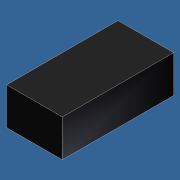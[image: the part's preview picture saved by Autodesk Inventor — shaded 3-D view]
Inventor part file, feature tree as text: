
AUTODESK INVENTOR PART (.ipt)
format: ipt  version: unknown  size: 157,184 bytes
history: native  units: mm
features: extrude x1, sketch x1
ambient origin geometry x8: Origin, YZ Plane, XZ Plane, XY Plane, X Axis, Y Axis, Z Axis, Center Point
feature tree (2):
  extrude  "Выдавливание1"  Depth=1.5mm
  sketch  "Эскиз1"
